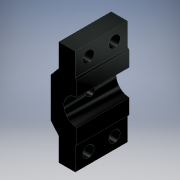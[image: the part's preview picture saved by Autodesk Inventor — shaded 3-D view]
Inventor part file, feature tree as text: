
AUTODESK INVENTOR PART (.ipt)
format: ipt  version: 2017 (Build 210142000, 142)  size: 188,928 bytes
history: native  units: mm
features: extrude x3, projected_geometry x3, sketch x2, chamfer x2
ambient origin geometry x8: Origin, YZ Plane, XZ Plane, XY Plane, X Axis, Y Axis, Z Axis, Center Point
bodies: Solid1 (feature_tree)
feature tree (10):
  extrude  "Extrusion1"  Depth=8.0mm
  sketch  "Sketch2"  dims[d2=5.0mm d3=5.0mm d4=0.5mm d5=7.0mm d6=7.0mm d8=5.0mm d9=5.0mm d10=0.0mm d11=7.0mm d12=7.0mm d13=6.0mm d14=6.0mm d15=8.0mm d17=24.468544mm d18=16.0mm d19=0.0mm d22=3.0mm d25=0.0mm d26=0.0mm d31=1.0mm d32=2.0mm d33=45.0deg d34=0.4mm d35=2.0mm d36=45.0deg d38=12.5mm d39=12.5mm d40=4.0mm d41=8.0mm d42=3.5mm d43=3.5mm d44=3.5mm d45=3.5mm d46=3.6mm d47=90.0deg d48=90.0deg d49=90.0deg d50=90.0deg d51=5.146447mm d52=28.503553mm d53=8.007005mm d54=0.0mm d55=0.0mm d56=1.5mm d57=0.0mm d58=16.0mm d59=6.0mm d60=10.0mm d61=14.0mm d62=16.0mm d63=15.9mm d64=16.0mm d65=8.0mm d66=22.0mm d67=23.353553mm d68=4.007005mm d69=12.007005mm d70=29.853553mm d71=15.0mm d72=0.0mm]
  extrude  "Extrusion3"  Depth=5.0mm
  chamfer  "Chamfer1"  Distance=0.5mm
  chamfer  "Chamfer2"  Distance=7.0mm
  extrude  "Extrusion5"  Depth=7.0mm
  sketch  "Sketch1"  dims[d0=8.0mm d1=8.0mm]
  projected_geometry  "Projected Loop1"
  projected_geometry  "Projected Loop2"
  projected_geometry  "Projected Loop3"
